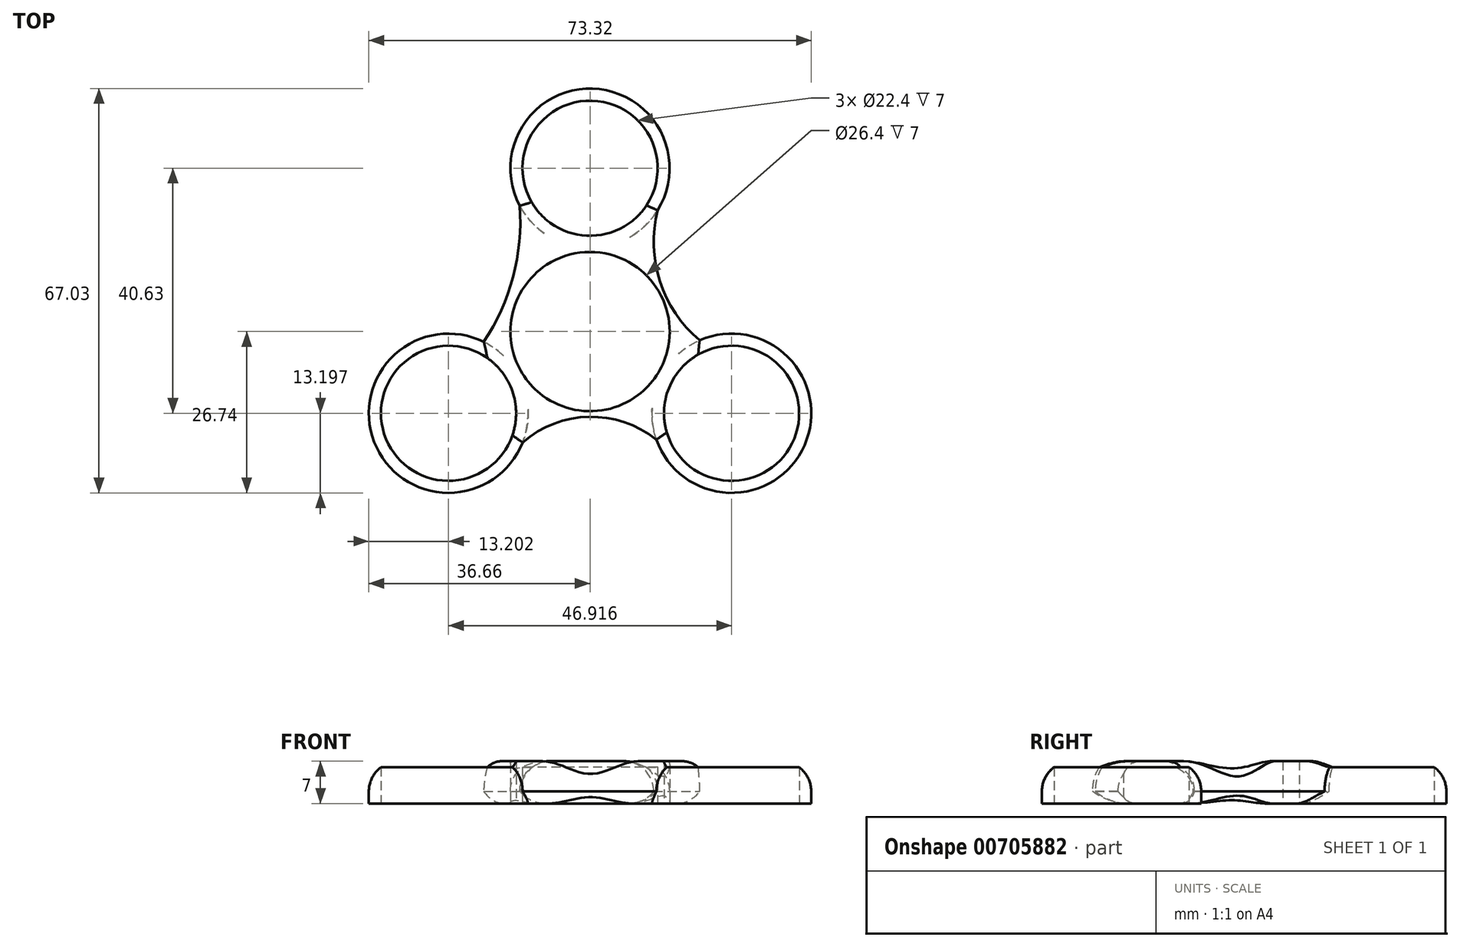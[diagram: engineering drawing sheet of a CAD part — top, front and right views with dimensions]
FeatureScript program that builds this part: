
annotation { "Feature Type Name" : "Feature", "Feature Type Description" : "" }
export const myFeature = defineFeature(function(context is Context, id is Id, definition is map)
    precondition{}
    {
        {
            var Q0;
            Q0=qCreatedBy(makeId("Top.planeOp"),FACE);
            var sketch = newSketch(context, id + "F0", { "sketchPlane" : qUnion([Q0])});
            skCircle(sketch, "E0", {"center": v(0, 0) * mm, "radius": 11.2 * mm});
            skCircle(sketch, "E1", {"center": v(0, 0) * mm, "radius": 13.2 * mm});
            skCircle(sketch, "E2", {"center": v(0, 27.09) * mm, "radius": 11.2 * mm});
            skArc(sketch, "E3", {"start": v(11.2, 20.11) * mm, "mid": v(0.43, 40.28) * mm, "end": v(-11.64, 20.86) * mm});
            skArc(sketch, "E4.1.0", {"start": v(-17.6, -1.7) * mm, "mid": v(-35.77, -18.3) * mm, "end": v(-11.18, -18.38) * mm});
            skCircle(sketch, "E4.1.1", {"center": v(-23.46, -13.54) * mm, "radius": 11.2 * mm});
            skArc(sketch, "E4.2.0", {"start": v(11, -17.91) * mm, "mid": v(35.56, -18.82) * mm, "end": v(18.18, -1.45) * mm});
            skCircle(sketch, "E4.2.1", {"center": v(23.46, -13.54) * mm, "radius": 11.2 * mm});
            skArc(sketch, "E5", {"start": v(-17.6, -1.7) * mm, "mid": v(-12.77, 9.09) * mm, "end": v(-11.64, 20.86) * mm});
            skArc(sketch, "E6", {"start": v(11, -17.91) * mm, "mid": v(-0.17, -14.13) * mm, "end": v(-11.18, -18.38) * mm});
            skArc(sketch, "E7", {"start": v(11.2, 20.11) * mm, "mid": v(11.57, 8.33) * mm, "end": v(18.18, -1.45) * mm});
            skSolve(sketch);
        }
        {
            var Q0;
            Q0 = qSketchRegion(id + "F0", true);
            extrude(context, id + "F1", {"entities" : qUnion([Q0]), "depth" : 7 * mm, "offsetDistance" : 25 * mm});
        }
        {
            var Q0;
            Q0=makeQuery(id+"F1.opExtrude","CAP_EDGE",EDGE,{"disambiguationData":[OSD([sQuery(id+"F0.wireOp",EDGE,"E5")])],"isStart":false});
            var Q1;
            Q1=makeQuery(id+"F1.opExtrude","CAP_EDGE",EDGE,{"disambiguationData":[OSD([sQuery(id+"F0.wireOp",EDGE,"E4.1.0")])],"isStart":false});
            var Q2;
            Q2=makeQuery(id+"F1.opExtrude","CAP_EDGE",EDGE,{"disambiguationData":[OSD([sQuery(id+"F0.wireOp",EDGE,"E6")])],"isStart":false});
            var Q3;
            Q3=makeQuery(id+"F1.opExtrude","CAP_EDGE",EDGE,{"disambiguationData":[OSD([sQuery(id+"F0.wireOp",EDGE,"E7")])],"isStart":false});
            var Q4;
            Q4=makeQuery(id+"F1.opExtrude","CAP_EDGE",EDGE,{"disambiguationData":[OSD([sQuery(id+"F0.wireOp",EDGE,"E4.2.0")])],"isStart":false});
            var Q5;
            Q5=makeQuery(id+"F1.opExtrude","CAP_EDGE",EDGE,{"disambiguationData":[OSD([sQuery(id+"F0.wireOp",EDGE,"E3")])],"isStart":false});
            fillet(context, id + "F2", {"entities" : qUnion([Q0, Q1, Q2, Q3, Q4, Q5]), "radius" : 5 * mm, "tangentPropagation" : true, "allowEdgeOverflow" : false});
        }
        {
            var Q0;
            Q0=makeQuery(id+"F1.opExtrude","CAP_EDGE",EDGE,{"disambiguationData":[OSD([sQuery(id+"F0.wireOp",EDGE,"E6")])],"isStart":true});
            var Q1;
            Q1=makeQuery(id+"F1.opExtrude","CAP_EDGE",EDGE,{"disambiguationData":[OSD([sQuery(id+"F0.wireOp",EDGE,"E5")])],"isStart":true});
            var Q2;
            Q2=makeQuery(id+"F1.opExtrude","CAP_EDGE",EDGE,{"disambiguationData":[OSD([sQuery(id+"F0.wireOp",EDGE,"E7")])],"isStart":true});
            fillet(context, id + "F3", {"entities" : qUnion([Q0, Q1, Q2]), "radius" : 5 * mm, "tangentPropagation" : true, "allowEdgeOverflow" : false});
        }
    });
